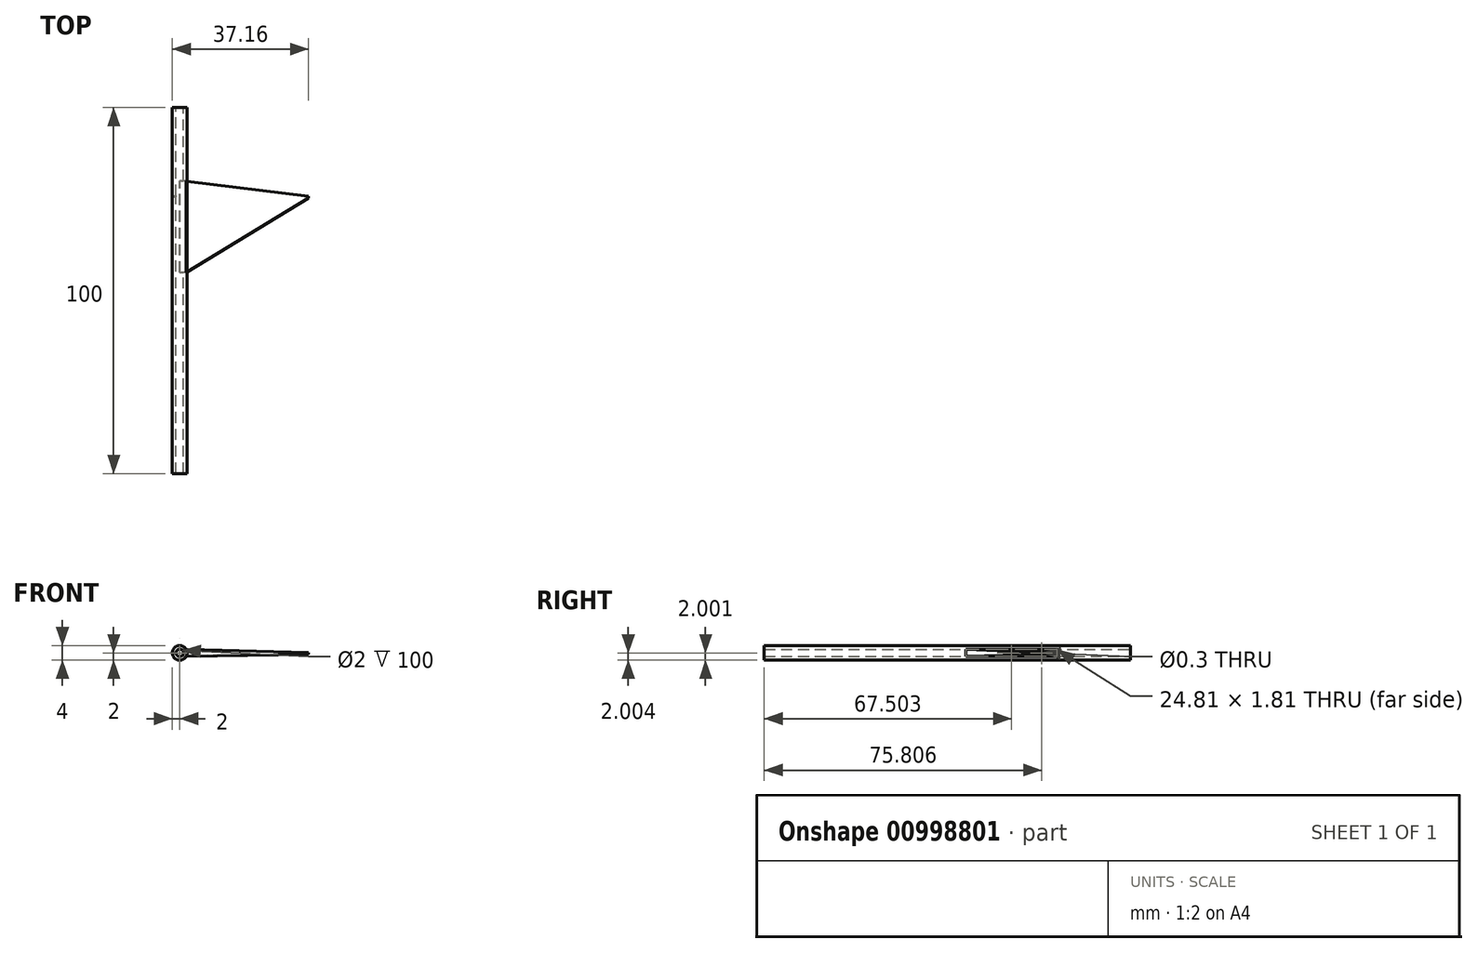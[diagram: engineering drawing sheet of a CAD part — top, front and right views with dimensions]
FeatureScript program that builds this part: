
annotation { "Feature Type Name" : "Feature", "Feature Type Description" : "" }
export const myFeature = defineFeature(function(context is Context, id is Id, definition is map)
    precondition{}
    {
        {
            var Q0;
            Q0=qCreatedBy(makeId("Front.planeOp"),FACE);
            var sketch = newSketch(context, id + "F0", { "sketchPlane" : qUnion([Q0])});
            skCircle(sketch, "E0", {"center": v(0, 0) * mm, "radius": 1 * mm});
            skCircle(sketch, "E1.0", {"center": v(0, 0) * mm, "radius": 2 * mm});
            skPoint(sketch, "E2", {"position": v(0, -1) * mm});
            skSolve(sketch);
        }
        {
            var Q0;
            Q0=qSketchRegion(id+"F0",true);
            extrude(context, id + "F1", {"entities" : qUnion([Q0]), "depth" : 100 * mm, "offsetDistance" : 25 * mm});
        }
        {
            var Q0;
            Q0=sQuery(id+"F0.wireOp",VERTEX,"E2");
            var Q1;
            Q1=sQuery(id+"F0.wireOp",EDGE,"E0");
            cPlane(context, id + "F2", {"entities" : qUnion([Q0, Q1]), "cplaneType" : CPlaneType.LINE_POINT, "offset" : 25 * mm, "width" : 150 * mm, "height" : 150 * mm});
        }
        {
            var Q0;
            Q0=qCreatedBy(id+"F2.planeOp",FACE);
            cPlane(context, id + "F3", {"entities" : qUnion([Q0]), "cplaneType" : CPlaneType.OFFSET, "offset" : 45 * mm, "width" : 150 * mm, "height" : 150 * mm});
        }
        {
            var Q0;
            Q0=qCreatedBy(id+"F3.planeOp",FACE);
            var sketch = newSketch(context, id + "F4", { "sketchPlane" : qUnion([Q0])});
            skLineSegment(sketch, "E3", {"start": v(0, -1) * mm, "end": v(1, -1) * mm, "construction": true});
            skLineSegment(sketch, "E4", {"start": v(0, 1) * mm, "end": v(1, 1) * mm, "construction": true});
            skLineSegment(sketch, "E5", {"start": v(1, -1) * mm, "end": v(1, 1) * mm});
            skSolve(sketch);
        }
        {
            var Q0;
            Q0=qSketchRegion(id+"F4",true);
            var Q1;
            Q1=sQuery(id+"F4.wireOp",EDGE,"E5");
            extrude(context, id + "F5", {"entities" : qUnion([Q0]), "bodyType" : ToolBodyType.SURFACE, "operationType" : NewBodyOperationType.REMOVE, "surfaceEntities" : qUnion([Q1]), "oppositeDirection" : true, "depth" : 25 * mm, "offsetDistance" : 25 * mm});
        }
        {
            var Q0;
            Q0=makeQuery(id+"F5.opExtrude","SWEPT_FACE",FACE,{"disambiguationData":[OSD([sQuery(id+"F4.wireOp",EDGE,"E5")])]});
            extrude(context, id + "F6", {"entities" : qUnion([Q0]), "operationType" : NewBodyOperationType.REMOVE, "oppositeDirection" : true, "depth" : 25 * mm, "offsetDistance" : 25 * mm, "hasSecondDirection" : true, "secondDirectionOppositeDirection" : false, "secondDirectionDepth" : 1 * mm});
        }
        {
            var Q0;
            Q0=makeQuery(id+"F6.boolean.opBoolean","INTERSECT",EDGE,{"derivedFrom":[makeQuery(id+"F1.opExtrude","SWEPT_FACE",FACE,{"disambiguationData":[OSD([sQuery(id+"F0.wireOp",EDGE,"E1.0")])]}),makeQuery(id+"F6.opExtrude","SWEPT_FACE",FACE,{"disambiguationData":[OSD([sQuery(id+"F4.wireOp",VERTEX,"E5.start")])]})]});
            var Q1;
            Q1=makeQuery(id+"F6.boolean.opBoolean","INTERSECT",EDGE,{"derivedFrom":[makeQuery(id+"F1.opExtrude","SWEPT_FACE",FACE,{"disambiguationData":[OSD([sQuery(id+"F0.wireOp",EDGE,"E1.0")])]}),makeQuery(id+"F6.opExtrude","SWEPT_FACE",FACE,{"disambiguationData":[OSD([sQuery(id+"F4.wireOp",VERTEX,"E5.end")])]})]});
            cPlane(context, id + "F7", {"entities" : qUnion([Q0, Q1]), "cplaneType" : CPlaneType.LINE_ANGLE, "offset" : 25 * mm, "angle" : 0 * degree, "width" : 150 * mm, "height" : 150 * mm});
        }
        {
            var Q0;
            Q0=qCreatedBy(id+"F7.planeOp",FACE);
            var sketch = newSketch(context, id + "F8", { "sketchPlane" : qUnion([Q0])});
            skLineSegment(sketch, "E6.bottom", {"start": v(-20, -1) * mm, "end": v(-45, -1) * mm});
            skLineSegment(sketch, "E6.top", {"start": v(-20, 1) * mm, "end": v(-45, 1) * mm});
            skLineSegment(sketch, "E6.left", {"start": v(-20, -1) * mm, "end": v(-20, 1) * mm});
            skLineSegment(sketch, "E6.right", {"start": v(-45, -1) * mm, "end": v(-45, 1) * mm});
            skLineSegment(sketch, "E7", {"start": v(-45, 0) * mm, "end": v(-20, 0) * mm});
            skLineSegment(sketch, "E8", {"start": v(-45, 0) * mm, "end": v(-41.17, 0) * mm});
            skLineSegment(sketch, "E9", {"start": v(-20, 0) * mm, "end": v(-24.2, 0) * mm});
            skSolve(sketch);
        }
        {
            var Q0;
            Q0=qSketchRegion(id+"F8",true);
            extrude(context, id + "F9", {"entities" : qUnion([Q0]), "depth" : 0.3 * mm, "offsetDistance" : 25 * mm});
        }
        {
            var Q0;
            Q0=makeQuery(id+"F9.opExtrude","CAP_FACE",FACE,{"disambiguationData":[OSD([sQuery(id+"F8.wireOp",EDGE,"E6.bottom"),sQuery(id+"F8.wireOp",EDGE,"E6.top"),sQuery(id+"F8.wireOp",EDGE,"E6.left"),sQuery(id+"F8.wireOp",EDGE,"E6.right")])],"isStart":false});
            var Q1;
            Q1=makeQuery(id+"F9.opExtrude","CAP_FACE",FACE,{"disambiguationData":[OSD([sQuery(id+"F8.wireOp",EDGE,"E6.bottom"),sQuery(id+"F8.wireOp",EDGE,"E6.top"),sQuery(id+"F8.wireOp",EDGE,"E6.left"),sQuery(id+"F8.wireOp",EDGE,"E6.right")])],"isStart":true});
            var Q2;
            Q2=makeQuery(id+"F9.opExtrude","SWEPT_BODY",BODY,{"disambiguationData":[OSD([sQuery(id+"F8.wireOp",EDGE,"E6.bottom"),sQuery(id+"F8.wireOp",EDGE,"E6.top"),sQuery(id+"F8.wireOp",EDGE,"E6.left"),sQuery(id+"F8.wireOp",EDGE,"E6.right")])]});
            shell(context, id + "F10", {"entities" : qUnion([Q0, Q1]), "parts" : qUnion([Q2]), "thickness" : 0.1 * mm});
        }
        {
            var Q0;
            Q0=sQuery(id+"F8.wireOp",VERTEX,"E9.end");
            var Q1;
            Q1=makeQuery(id+"F1.opExtrude","SWEPT_BODY",BODY,{"disambiguationData":[OSD([sQuery(id+"F0.wireOp",EDGE,"E0"),sQuery(id+"F0.wireOp",EDGE,"E1.0")])]});
            hole(context, id + "F11", {"style" : HoleStyle.SIMPLE, "endStyle" : HoleEndStyle.THROUGH, "holeDiameter" : 0.3 * mm, "majorDiameter" : 5 * mm, "isTappedThrough" : true, "tappedDepth" : 12 * mm, "tapClearance" : 3, "locations" : qUnion([Q0]), "scope" : qUnion([Q1])});
        }
        {
            var Q0;
            Q0=qCreatedBy(id+"F7.planeOp",FACE);
            cPlane(context, id + "F12", {"entities" : qUnion([Q0]), "cplaneType" : CPlaneType.OFFSET, "offset" : 33.43 * mm, "width" : 150 * mm, "height" : 150 * mm});
        }
        {
            var Q0;
            Q0=qCreatedBy(id+"F12.planeOp",FACE);
            var sketch = newSketch(context, id + "F13", { "sketchPlane" : qUnion([Q0])});
            skLineSegment(sketch, "E10.bottom", {"start": v(-24.25, -0.55) * mm, "end": v(-24.79, -0.55) * mm});
            skLineSegment(sketch, "E10.top", {"start": v(-24.25, 0) * mm, "end": v(-24.79, 0) * mm});
            skLineSegment(sketch, "E10.left", {"start": v(-24.25, -0.55) * mm, "end": v(-24.25, 0) * mm});
            skLineSegment(sketch, "E10.right", {"start": v(-24.79, -0.55) * mm, "end": v(-24.79, 0) * mm});
            skSolve(sketch);
        }
        {
            var Q0;
            Q0=makeQuery(id+"F9.opExtrude","CAP_FACE",FACE,{"disambiguationData":[OSD([sQuery(id+"F8.wireOp",EDGE,"E6.bottom"),sQuery(id+"F8.wireOp",EDGE,"E6.top"),sQuery(id+"F8.wireOp",EDGE,"E6.left"),sQuery(id+"F8.wireOp",EDGE,"E6.right")])],"isStart":false});
            var sketch = newSketch(context, id + "F14", { "sketchPlane" : qUnion([Q0])});
            skLineSegment(sketch, "E11.bottom", {"start": v(-44.9, -0.9) * mm, "end": v(-20.1, -0.9) * mm});
            skLineSegment(sketch, "E11.top", {"start": v(-44.9, 0.9) * mm, "end": v(-20.1, 0.9) * mm});
            skLineSegment(sketch, "E11.left", {"start": v(-44.9, -0.9) * mm, "end": v(-44.9, 0.9) * mm});
            skLineSegment(sketch, "E11.right", {"start": v(-20.1, -0.9) * mm, "end": v(-20.1, 0.9) * mm});
            skSolve(sketch);
        }
        {
            var Q0;
            Q0=makeQuery(id+"F14.imprint","IMPRINT",FACE,{"disambiguationData":[TD([[makeQuery(id+"F14.imprint","IMPRINT",EDGE,{"derivedFrom":sQuery(id+"F14.wireOp",EDGE,"E11.bottom")}),-1.0]])]});
            var Q1;
            Q1=makeQuery(id+"F13.imprint","IMPRINT",FACE,{"disambiguationData":[TD([[makeQuery(id+"F13.imprint","IMPRINT",EDGE,{"derivedFrom":sQuery(id+"F13.wireOp",EDGE,"E10.bottom")}),-1.0]])]});
            loft(context, id + "F15", {"sheetProfilesArray" : [{ "sheetProfileEntities" : qUnion([Q0]) }, { "sheetProfileEntities" : qUnion([Q1]) }]});
        }
        {
            var Q0;
            Q0=makeQuery(id+"F15.opLoft","CAP_FACE",FACE,{"disambiguationData":[OSD([makeQuery(id+"F13.imprint","IMPRINT",FACE,{"disambiguationData":[TD([[makeQuery(id+"F13.imprint","IMPRINT",EDGE,{"derivedFrom":sQuery(id+"F13.wireOp",EDGE,"E10.bottom")}),-1.0]])]})])],"isStart":true});
            var Q1;
            Q1=makeQuery(id+"F15.opLoft","CAP_FACE",FACE,{"disambiguationData":[OSD([makeQuery(id+"F14.imprint","IMPRINT",FACE,{"disambiguationData":[TD([[makeQuery(id+"F14.imprint","IMPRINT",EDGE,{"derivedFrom":sQuery(id+"F14.wireOp",EDGE,"E11.bottom")}),-1.0]])]})])],"isStart":true});
            shell(context, id + "F16", {"entities" : qUnion([Q0, Q1]), "thickness" : 0.1 * mm});
        }
    });
